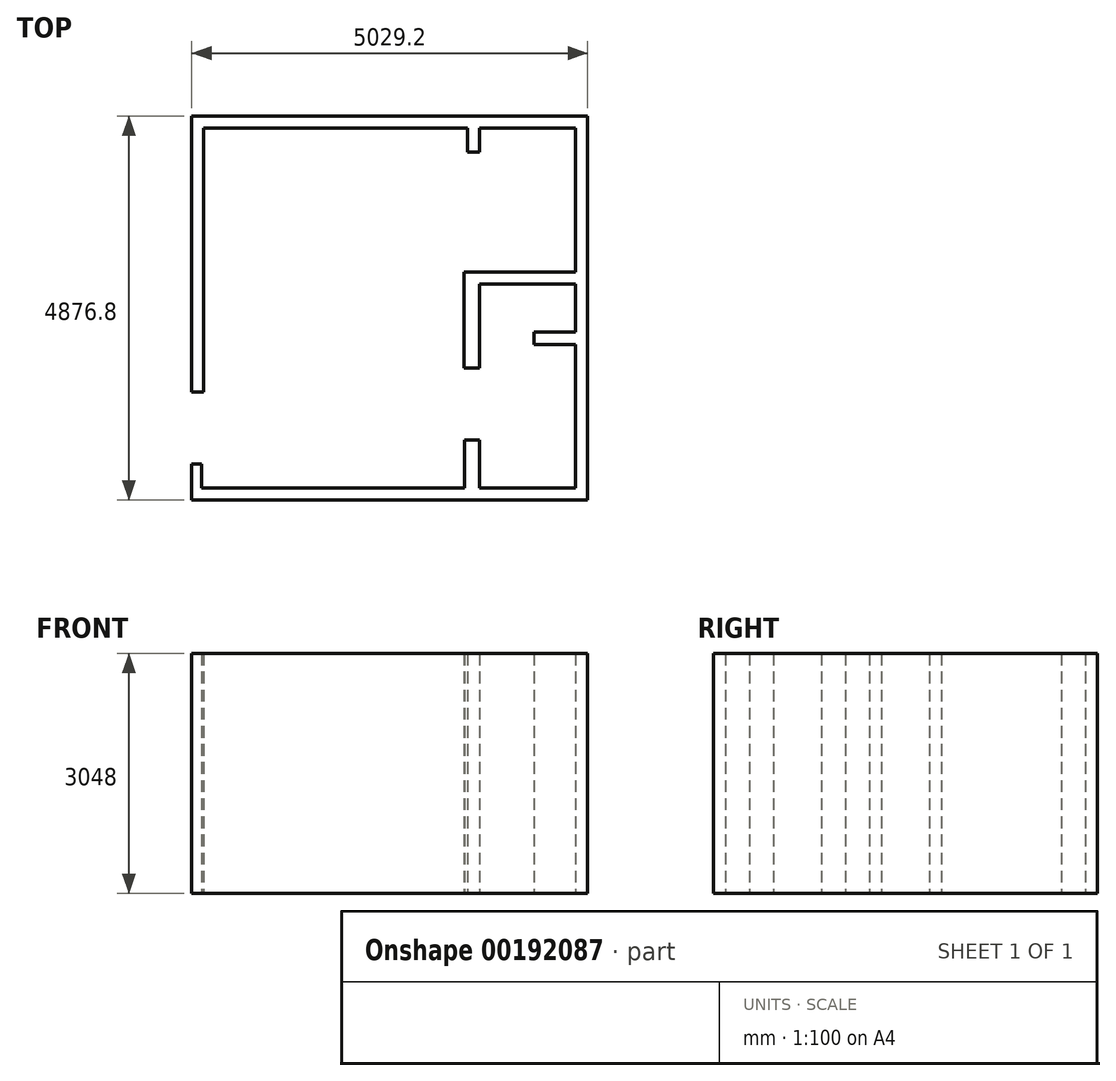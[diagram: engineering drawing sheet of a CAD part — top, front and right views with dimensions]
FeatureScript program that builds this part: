
annotation { "Feature Type Name" : "Feature", "Feature Type Description" : "" }
export const myFeature = defineFeature(function(context is Context, id is Id, definition is map)
    precondition{}
    {
        {
            var Q0;
            Q0=qCreatedBy(makeId("Top.planeOp"),FACE);
            var sketch = newSketch(context, id + "F0", { "sketchPlane" : qUnion([Q0])});
            skLineSegment(sketch, "E0", {"start": v(-152.4, 3899.73) * mm, "end": v(0, 3899.73) * mm});
            skLineSegment(sketch, "E1", {"start": v(-108.68, -672.27) * mm, "end": v(-177.8, -672.27) * mm});
            skLineSegment(sketch, "E2", {"start": v(-177.8, -672.27) * mm, "end": v(-177.8, -367.47) * mm});
            skLineSegment(sketch, "E3", {"start": v(-152.4, 3899.73) * mm, "end": v(-152.4, 546.93) * mm});
            skLineSegment(sketch, "E4", {"start": v(-152.4, 546.93) * mm, "end": v(-304.8, 546.93) * mm});
            skLineSegment(sketch, "E5", {"start": v(-304.8, 546.93) * mm, "end": v(-304.8, 4052.13) * mm});
            skLineSegment(sketch, "E6", {"start": v(-304.8, 4052.13) * mm, "end": v(0, 4052.13) * mm});
            skLineSegment(sketch, "E7", {"start": v(0, 4052.13) * mm, "end": v(3352.8, 4052.13) * mm});
            skLineSegment(sketch, "E8", {"start": v(-177.8, -367.47) * mm, "end": v(-304.8, -367.47) * mm});
            skLineSegment(sketch, "E9", {"start": v(-304.8, -367.47) * mm, "end": v(-304.8, -824.67) * mm});
            skLineSegment(sketch, "E10", {"start": v(-304.8, -824.67) * mm, "end": v(3352.8, -824.67) * mm});
            skLineSegment(sketch, "E11", {"start": v(3352.8, 851.73) * mm, "end": v(3150.6, 851.73) * mm});
            skLineSegment(sketch, "E12", {"start": v(3150.6, 851.73) * mm, "end": v(3150.6, 2070.93) * mm});
            skLineSegment(sketch, "E13", {"start": v(3150.6, 2070.93) * mm, "end": v(3352.8, 2070.93) * mm});
            skLineSegment(sketch, "E14", {"start": v(3352.8, -62.67) * mm, "end": v(3156.7, -62.67) * mm});
            skLineSegment(sketch, "E15", {"start": v(3156.7, -62.67) * mm, "end": v(3156.7, -672.27) * mm});
            skLineSegment(sketch, "E16", {"start": v(3156.7, -672.27) * mm, "end": v(-108.68, -672.27) * mm});
            skLineSegment(sketch, "E17", {"start": v(0, 3899.73) * mm, "end": v(3200.4, 3899.73) * mm});
            skLineSegment(sketch, "E18", {"start": v(3352.8, 4052.13) * mm, "end": v(4724.4, 4052.13) * mm});
            skLineSegment(sketch, "E19", {"start": v(4724.4, 4052.13) * mm, "end": v(4724.4, -824.67) * mm});
            skLineSegment(sketch, "E20", {"start": v(4724.4, -824.67) * mm, "end": v(3352.8, -824.67) * mm});
            skLineSegment(sketch, "E21", {"start": v(3352.8, -672.27) * mm, "end": v(4572, -672.27) * mm});
            skLineSegment(sketch, "E22", {"start": v(4572, 3899.73) * mm, "end": v(3352.8, 3899.73) * mm});
            skLineSegment(sketch, "E23", {"start": v(3352.8, 2070.93) * mm, "end": v(4572, 2070.93) * mm});
            skLineSegment(sketch, "E24", {"start": v(4572, 1918.53) * mm, "end": v(3352.8, 1918.53) * mm});
            skLineSegment(sketch, "E25", {"start": v(4042.9, 1308.93) * mm, "end": v(4572, 1308.93) * mm});
            skLineSegment(sketch, "E26", {"start": v(3200.4, 3899.73) * mm, "end": v(3200.4, 3594.93) * mm});
            skLineSegment(sketch, "E27", {"start": v(3200.4, 3594.93) * mm, "end": v(3352.8, 3594.93) * mm});
            skLineSegment(sketch, "E28", {"start": v(3352.8, 3594.93) * mm, "end": v(3352.8, 3899.73) * mm});
            skLineSegment(sketch, "E29", {"start": v(4042.9, 1308.93) * mm, "end": v(4042.9, 1150.73) * mm});
            skLineSegment(sketch, "E30", {"start": v(4042.9, 1150.73) * mm, "end": v(4572, 1150.73) * mm});
            skLineSegment(sketch, "E31", {"start": v(3352.8, 1918.53) * mm, "end": v(3352.8, 851.73) * mm});
            skLineSegment(sketch, "E32", {"start": v(4572, 1308.93) * mm, "end": v(4572, 1918.53) * mm});
            skLineSegment(sketch, "E33", {"start": v(4572, 1150.73) * mm, "end": v(4572, -672.27) * mm});
            skLineSegment(sketch, "E34", {"start": v(3352.8, -62.67) * mm, "end": v(3352.8, -672.27) * mm});
            skLineSegment(sketch, "E35", {"start": v(4572, 3899.73) * mm, "end": v(4572, 2070.93) * mm});
            skSolve(sketch);
        }
        {
            var Q0;
            Q0 = qSketchRegion(id + "F0", true);
            extrude(context, id + "F1", {"entities" : qUnion([Q0]), "depth" : 3048 * mm});
        }
    });
